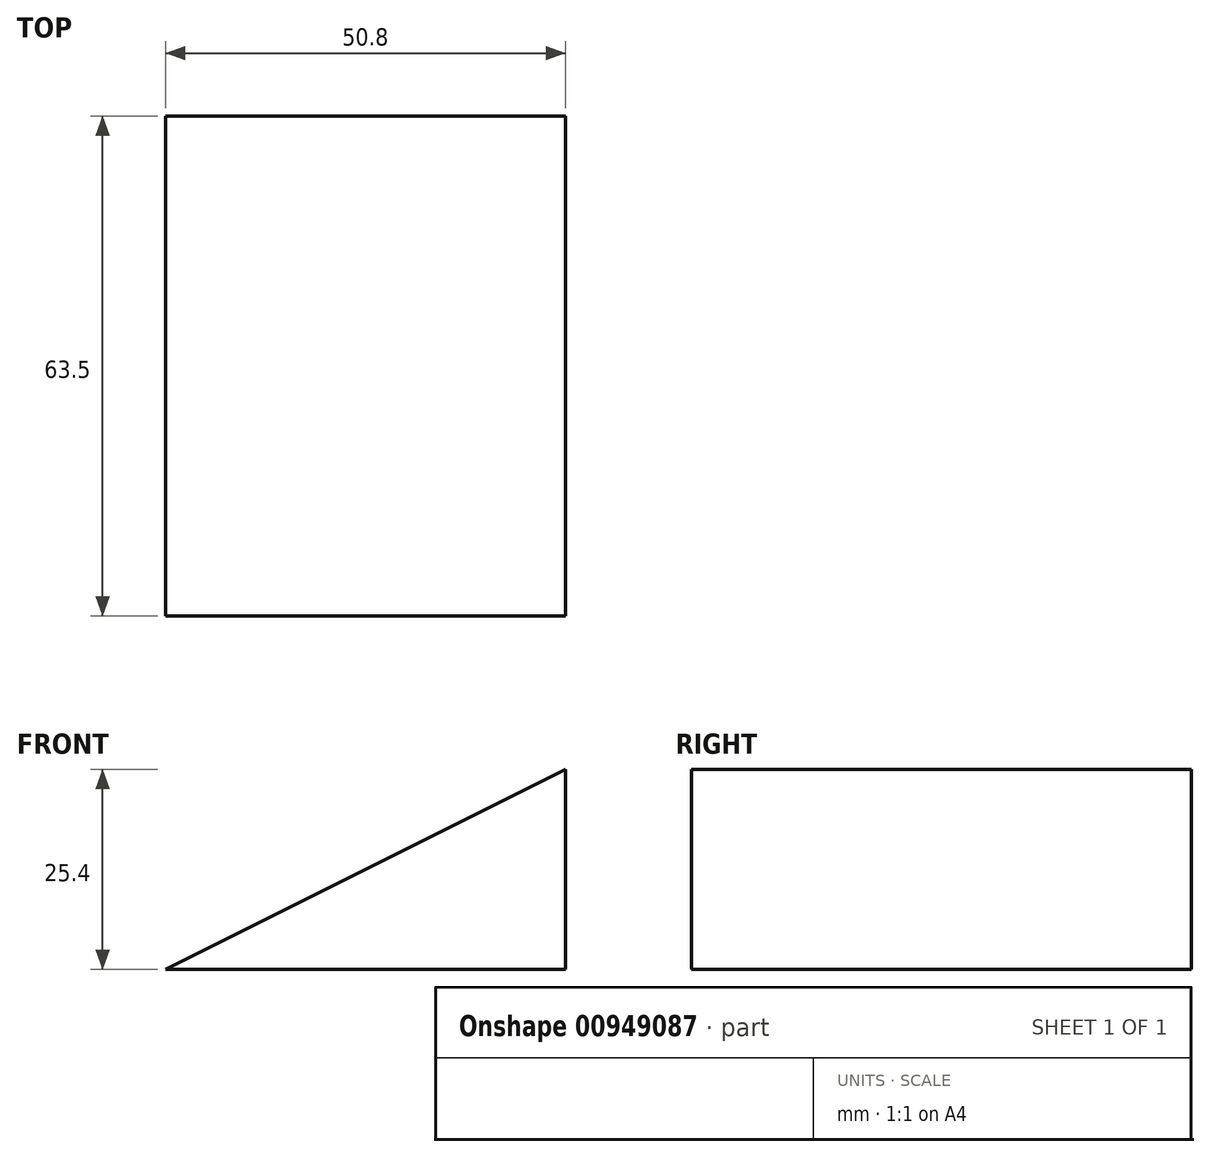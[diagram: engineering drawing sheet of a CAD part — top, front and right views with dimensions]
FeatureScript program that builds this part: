
annotation { "Feature Type Name" : "Feature", "Feature Type Description" : "" }
export const myFeature = defineFeature(function(context is Context, id is Id, definition is map)
    precondition{}
    {
        {
            var Q0;
            Q0=qCreatedBy(makeId("Front.planeOp"),FACE);
            var sketch = newSketch(context, id + "F0", { "sketchPlane" : qUnion([Q0])});
            skLineSegment(sketch, "E0", {"start": v(23.02, 7.32) * mm, "end": v(23.02, -18.08) * mm});
            skLineSegment(sketch, "E1", {"start": v(23.02, -18.08) * mm, "end": v(-27.78, -18.08) * mm});
            skLineSegment(sketch, "E2", {"start": v(23.02, 7.32) * mm, "end": v(-27.78, -18.08) * mm});
            skSolve(sketch);
        }
        {
            var Q0;
            Q0 = qSketchRegion(id + "F0", true);
            extrude(context, id + "F1", {"entities" : qUnion([Q0]), "depth" : 63.5 * mm, "offsetDistance" : 25.4 * mm});
        }
    });
